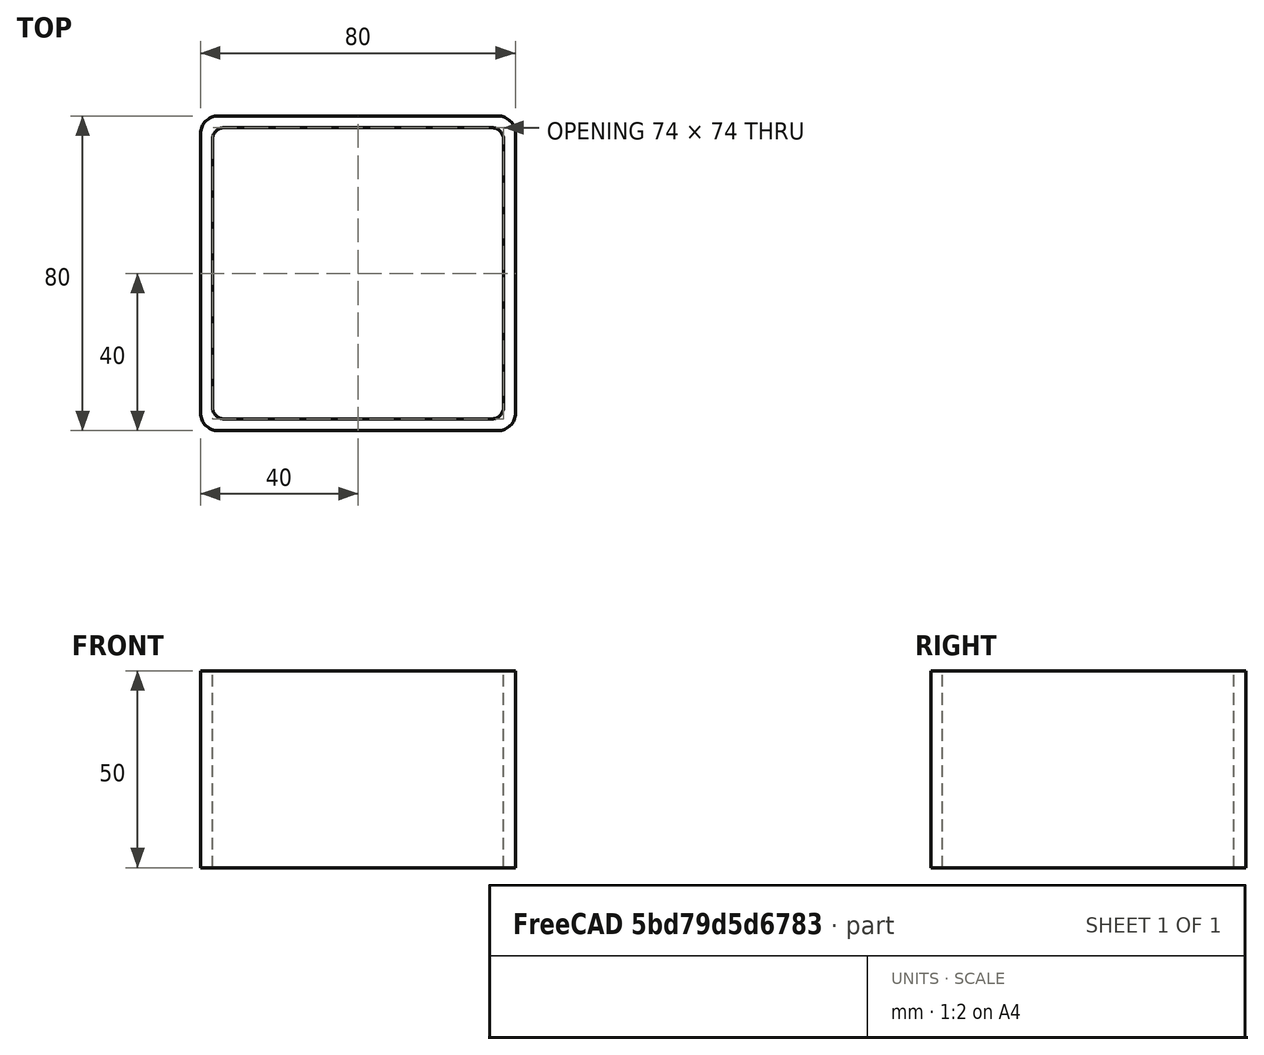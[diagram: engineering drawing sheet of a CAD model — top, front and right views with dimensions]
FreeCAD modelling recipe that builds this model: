
FCSTD DOCUMENT  (FreeCAD 0.15R4671 (Git))
Label: Square hollow section 80x80x3 EN10219 S235JRH
License: All rights reserved
LicenseURL: http://en.wikipedia.org/wiki/All_rights_reserved
objects: Sketcher::SketchObject×1, Part::Extrusion×1
note: 2 computed .brp shape members not serialized (recipe doc carries the construction recipe); baked Part::Feature solids carry a one-line shape summary decoded from their .brp

FEATURE [Sketcher::SketchObject] Sketch
  sketch-geometry (16):
    g0: LineSegment StartX=-34 StartY=37 StartZ=0 EndX=34 EndY=37 EndZ=0
    g1: LineSegment StartX=37 StartY=34 StartZ=0 EndX=37 EndY=-34 EndZ=0
    g2: LineSegment StartX=34 StartY=-37 StartZ=0 EndX=-34 EndY=-37 EndZ=0
    g3: LineSegment StartX=-37 StartY=-34 StartZ=0 EndX=-37 EndY=34 EndZ=0
    g4: LineSegment StartX=-35.5 StartY=40 StartZ=0 EndX=35.5 EndY=40 EndZ=0
    g5: LineSegment StartX=40 StartY=35.5 StartZ=0 EndX=40 EndY=-35.5 EndZ=0
    g6: LineSegment StartX=35.5 StartY=-40 StartZ=0 EndX=-35.5 EndY=-40 EndZ=0
    g7: LineSegment StartX=-40 StartY=-35.5 StartZ=0 EndX=-40 EndY=35.5 EndZ=0
    g8: ArcOfCircle CenterX=-34 CenterY=34 CenterZ=0 NormalX=0 NormalY=0 NormalZ=1 Radius=3 StartAngle=1.5708 EndAngle=3.14159
    g9: ArcOfCircle CenterX=34 CenterY=34 CenterZ=0 NormalX=0 NormalY=0 NormalZ=1 Radius=3 StartAngle=0 EndAngle=1.5708
    g10: ArcOfCircle CenterX=34 CenterY=-34 CenterZ=0 NormalX=0 NormalY=0 NormalZ=1 Radius=3 StartAngle=4.71239 EndAngle=6.28319
    g11: ArcOfCircle CenterX=-34 CenterY=-34 CenterZ=0 NormalX=0 NormalY=0 NormalZ=1 Radius=3 StartAngle=3.14159 EndAngle=4.71239
    g12: ArcOfCircle CenterX=35.5 CenterY=35.5 CenterZ=0 NormalX=0 NormalY=0 NormalZ=1 Radius=4.5 StartAngle=0 EndAngle=1.5708
    g13: ArcOfCircle CenterX=35.5 CenterY=-35.5 CenterZ=0 NormalX=0 NormalY=0 NormalZ=1 Radius=4.5 StartAngle=4.71239 EndAngle=6.28319
    g14: ArcOfCircle CenterX=-35.5 CenterY=-35.5 CenterZ=0 NormalX=0 NormalY=0 NormalZ=1 Radius=4.5 StartAngle=3.14159 EndAngle=4.71239
    g15: ArcOfCircle CenterX=-35.5 CenterY=35.5 CenterZ=0 NormalX=0 NormalY=0 NormalZ=1 Radius=4.5 StartAngle=1.5708 EndAngle=3.14159
  constraints (36):
    c: Horizontal(g2)
    c: Vertical(g3)
    c: Horizontal(g6)
    c: Vertical(g7)
    c: Tangent(g3,g8) = 1.5708
    c: Tangent(g0,g8) = 1.5708
    c: Tangent(g0,g9) = 1.5708
    c: Tangent(g1,g9) = 1.5708
    c: Tangent(g1,g10) = 1.5708
    c: Tangent(g2,g10) = 1.5708
    c: Tangent(g2,g11) = 1.5708
    c: Tangent(g3,g11) = 1.5708
    c: Tangent(g4,g12) = 1.5708
    c: Tangent(g5,g12) = 1.5708
    c: Tangent(g5,g13) = 1.5708
    c: Tangent(g6,g13) = 1.5708
    c: Tangent(g6,g14) = 1.5708
    c: Tangent(g7,g14) = 1.5708
    c: Tangent(g7,g15) = 1.5708
    c: Tangent(g4,g15) = 1.5708
    c: Equal(g9,g8)
    c: Equal(g9,g11)
    c: Equal(g9,g10)
    c: Equal(g12,g15)
    c: Equal(g12,g14)
    c: Equal(g12,g13)
    c: Symmetric(g4,g6,g-1)
    c: Symmetric(g7,g5,g-2)
    c: DistanceY(g4,g6) = -80
    c: DistanceX(g7,g5) = 80
    c: Symmetric(g3,g1,g-2)
    c: Symmetric(g0,g2,g-1)
    c: DistanceY(g0,g4) = 3
    c: DistanceX(g5,g1) = -3
    c: Radius(g9) = 3
    c: Radius(g12) = 4.5
FEATURE [Part::Extrusion] Extrude  label="Square hollow section 80x80x3 EN10219 S235JRH"
  Base = -> Sketch
  Dir = (0,0,50)
  Solid = true
